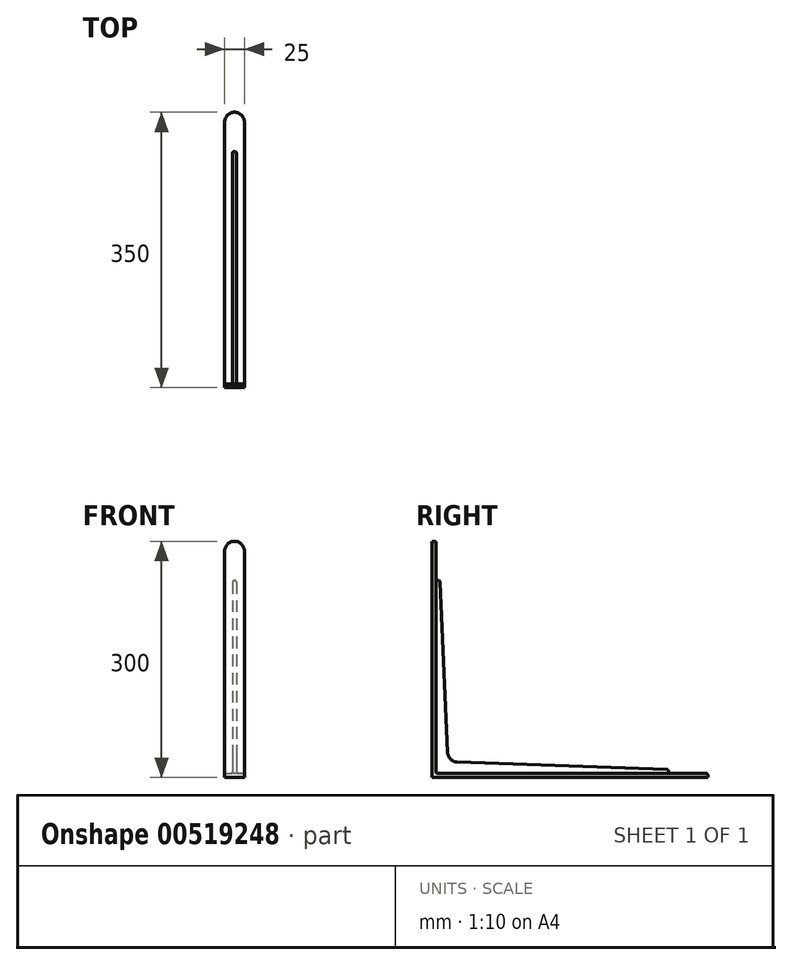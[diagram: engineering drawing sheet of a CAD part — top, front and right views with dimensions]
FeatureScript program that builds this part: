
annotation { "Feature Type Name" : "Feature", "Feature Type Description" : "" }
export const myFeature = defineFeature(function(context is Context, id is Id, definition is map)
    precondition{}
    {
        {
            var Q0;
            Q0=qCreatedBy(makeId("Right.planeOp"),FACE);
            var sketch = newSketch(context, id + "F0", { "sketchPlane" : qUnion([Q0])});
            skLineSegment(sketch, "E0.bottom", {"start": v(0, 0) * mm, "end": v(350, 0) * mm});
            skLineSegment(sketch, "E0.top", {"start": v(0, 300) * mm, "end": v(5, 300) * mm});
            skLineSegment(sketch, "E0.left", {"start": v(0, 0) * mm, "end": v(0, 300) * mm});
            skLineSegment(sketch, "E0.right", {"start": v(350, 0) * mm, "end": v(350, 5) * mm});
            skLineSegment(sketch, "E1.top", {"start": v(350, 5) * mm, "end": v(5, 5) * mm});
            skLineSegment(sketch, "E1.right", {"start": v(5, 300) * mm, "end": v(5, 5) * mm});
            skSolve(sketch);
        }
        {
            var Q0;
            Q0=qSketchRegion(id+"F0",true);
            extrude(context, id + "F1", {"entities" : qUnion([Q0]), "oppositeDirection" : true, "depth" : 25 * mm, "offsetDistance" : 25 * mm});
        }
        {
            var Q0;
            Q0=qCreatedBy(makeId("Right.planeOp"),FACE);
            cPlane(context, id + "F2", {"entities" : qUnion([Q0]), "cplaneType" : CPlaneType.OFFSET, "offset" : 10 * mm, "oppositeDirection" : true, "width" : 150 * mm, "height" : 150 * mm});
        }
        {
            var Q0;
            Q0=qCreatedBy(id+"F2.planeOp",FACE);
            var sketch = newSketch(context, id + "F3", { "sketchPlane" : qUnion([Q0])});
            skLineSegment(sketch, "E2", {"start": v(0, 0) * mm, "end": v(95.79, 95.79) * mm, "construction": true});
            skLineSegment(sketch, "E3", {"start": v(0, 0) * mm, "end": v(0, 250) * mm, "construction": true});
            skLineSegment(sketch, "E4", {"start": v(0, 250) * mm, "end": v(5, 250) * mm, "construction": true});
            skLineSegment(sketch, "E5", {"start": v(5, 250) * mm, "end": v(10, 250) * mm});
            skLineSegment(sketch, "E6", {"start": v(10, 250) * mm, "end": v(20, 20) * mm});
            skLineSegment(sketch, "E7", {"start": v(20, 20) * mm, "end": v(300, 10) * mm});
            skLineSegment(sketch, "E8", {"start": v(300, 10) * mm, "end": v(300, 5) * mm});
            skLineSegment(sketch, "E9", {"start": v(300, 5) * mm, "end": v(300, 0) * mm, "construction": true});
            skLineSegment(sketch, "E10", {"start": v(300, 0) * mm, "end": v(0, 0) * mm, "construction": true});
            skLineSegment(sketch, "E11", {"start": v(5, 250) * mm, "end": v(5, 5) * mm});
            skLineSegment(sketch, "E12", {"start": v(5, 5) * mm, "end": v(300, 5) * mm});
            skSolve(sketch);
        }
        {
            var Q0;
            Q0=qSketchRegion(id+"F3",true);
            extrude(context, id + "F4", {"entities" : qUnion([Q0]), "operationType" : NewBodyOperationType.ADD, "oppositeDirection" : true, "depth" : 5 * mm, "offsetDistance" : 25 * mm});
        }
        {
            var Q0;
            Q0=makeQuery(id+"F1.opExtrude","CAP_EDGE",EDGE,{"disambiguationData":[OSD([sQuery(id+"F0.wireOp",EDGE,"E0.top")])],"isStart":true});
            var Q1;
            Q1=makeQuery(id+"F1.opExtrude","CAP_EDGE",EDGE,{"disambiguationData":[OSD([sQuery(id+"F0.wireOp",EDGE,"E0.top")])],"isStart":false});
            var Q2;
            Q2=makeQuery(id+"F1.opExtrude","CAP_EDGE",EDGE,{"disambiguationData":[OSD([sQuery(id+"F0.wireOp",EDGE,"E0.right")])],"isStart":false});
            var Q3;
            Q3=makeQuery(id+"F1.opExtrude","CAP_EDGE",EDGE,{"disambiguationData":[OSD([sQuery(id+"F0.wireOp",EDGE,"E0.right")])],"isStart":true});
            var Q4;
            Q4=makeQuery(id+"F4.opExtrude","SWEPT_EDGE",EDGE,{"disambiguationData":[OSD([sQuery(id+"F3.wireOp",EDGE,"E6"),sQuery(id+"F3.wireOp",EDGE,"E7")])]});
            fillet(context, id + "F5", {"entities" : qUnion([Q0, Q1, Q2, Q3, Q4]), "radius" : 12.5 * mm, "tangentPropagation" : true, "allowEdgeOverflow" : false});
        }
        {
            var Q0;
            Q0=makeQuery(id+"F1.opExtrude","SWEPT_FACE",FACE,{"disambiguationData":[OSD([sQuery(id+"F0.wireOp",EDGE,"E1.right")])]});
            var Q1;
            Q1=makeQuery(id+"F4.opExtrude","SWEPT_FACE",FACE,{"disambiguationData":[OSD([sQuery(id+"F3.wireOp",EDGE,"E6")])]});
            var Q2;
            Q2=makeQuery(id+"F4.opExtrude","CAP_FACE",FACE,{"disambiguationData":[OSD([sQuery(id+"F3.wireOp",EDGE,"E5"),sQuery(id+"F3.wireOp",EDGE,"E6"),sQuery(id+"F3.wireOp",EDGE,"E7"),sQuery(id+"F3.wireOp",EDGE,"E8"),sQuery(id+"F3.wireOp",EDGE,"E11"),sQuery(id+"F3.wireOp",EDGE,"E12")])],"isStart":false});
            var Q3;
            Q3=makeQuery(id+"F4.opExtrude","CAP_FACE",FACE,{"disambiguationData":[OSD([sQuery(id+"F3.wireOp",EDGE,"E5"),sQuery(id+"F3.wireOp",EDGE,"E6"),sQuery(id+"F3.wireOp",EDGE,"E7"),sQuery(id+"F3.wireOp",EDGE,"E8"),sQuery(id+"F3.wireOp",EDGE,"E11"),sQuery(id+"F3.wireOp",EDGE,"E12")])],"isStart":true});
            var Q4;
            Q4=makeQuery(id+"F1.opExtrude","SWEPT_FACE",FACE,{"disambiguationData":[OSD([sQuery(id+"F0.wireOp",EDGE,"E1.top")])]});
            var Q5;
            Q5=makeQuery(id+"F4.opExtrude","SWEPT_FACE",FACE,{"disambiguationData":[OSD([sQuery(id+"F3.wireOp",EDGE,"E8")])]});
            fillet(context, id + "F6", {"entities" : qUnion([Q0, Q1, Q2, Q3, Q4, Q5]), "radius" : 2 * mm, "tangentPropagation" : true, "allowEdgeOverflow" : false});
        }
    });
